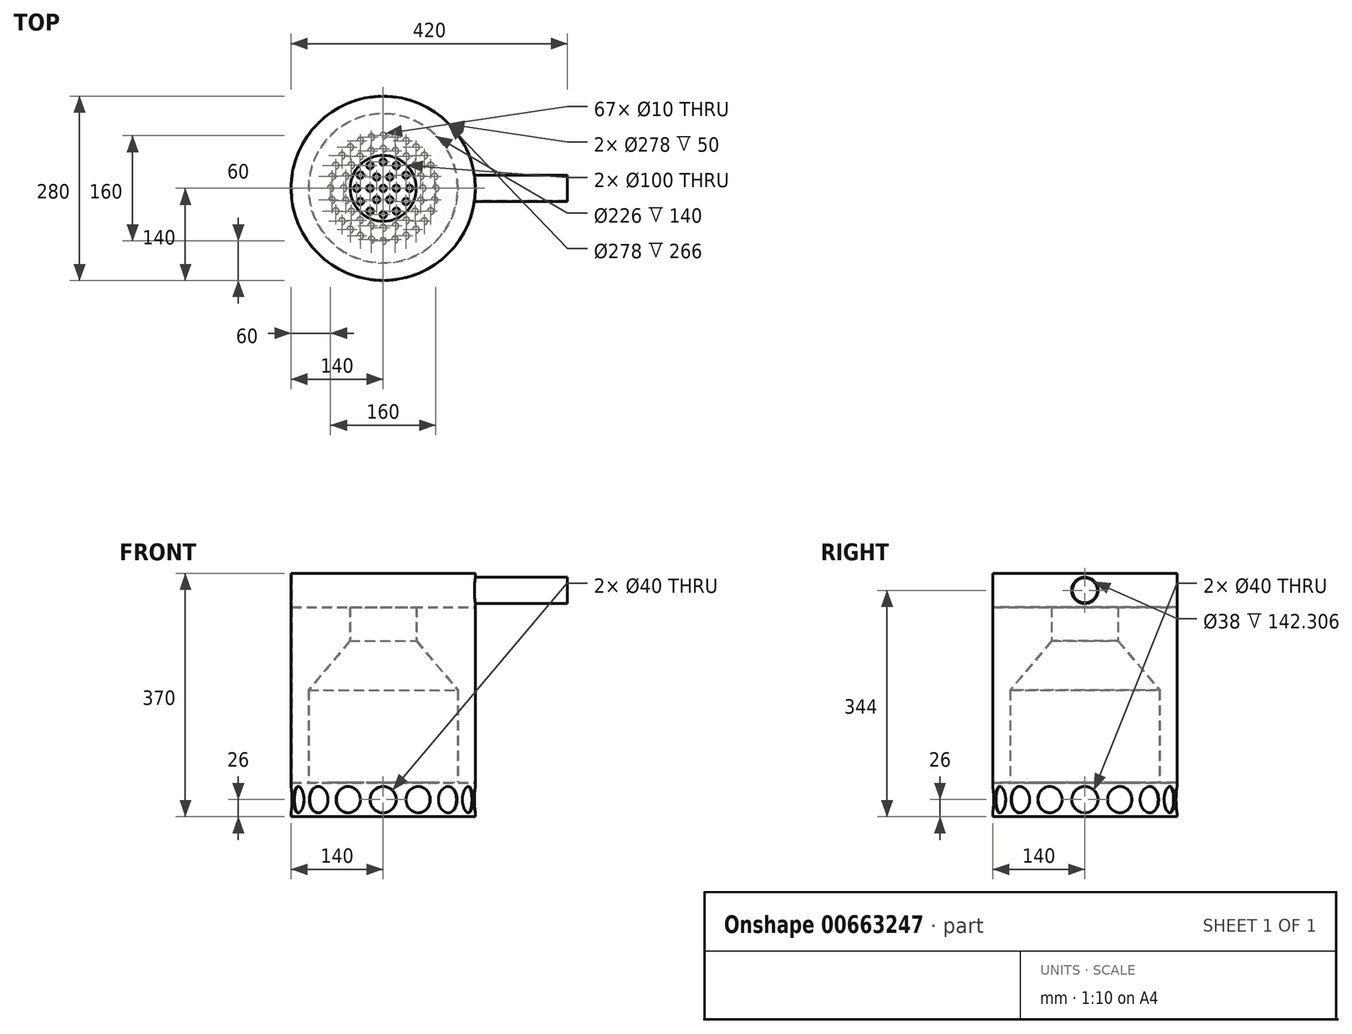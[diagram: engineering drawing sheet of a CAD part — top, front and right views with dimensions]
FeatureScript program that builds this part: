
annotation { "Feature Type Name" : "Feature", "Feature Type Description" : "" }
export const myFeature = defineFeature(function(context is Context, id is Id, definition is map)
    precondition{}
    {
        {
            var Q0;
            Q0=qCreatedBy(makeId("Front.planeOp"),FACE);
            var sketch = newSketch(context, id + "F0", { "sketchPlane" : qUnion([Q0])});
            skLineSegment(sketch, "E0", {"start": v(0, 0) * mm, "end": v(140, 0) * mm});
            skLineSegment(sketch, "E1", {"start": v(140, 0) * mm, "end": v(140, 370) * mm});
            skLineSegment(sketch, "E2", {"start": v(140, 370) * mm, "end": v(50, 370) * mm});
            skLineSegment(sketch, "E3.0", {"start": v(139, 369) * mm, "end": v(50, 369) * mm});
            skLineSegment(sketch, "E3.1", {"start": v(139, 1) * mm, "end": v(139, 369) * mm});
            skLineSegment(sketch, "E3.2", {"start": v(0, 1) * mm, "end": v(139, 1) * mm});
            skLineSegment(sketch, "E4", {"start": v(50, 370) * mm, "end": v(50, 369) * mm});
            skLineSegment(sketch, "E5", {"start": v(0, 1) * mm, "end": v(0, 0) * mm});
            skLineSegment(sketch, "E6", {"start": v(0, 51) * mm, "end": v(139, 51) * mm});
            skLineSegment(sketch, "E7", {"start": v(0, 51) * mm, "end": v(0, 52) * mm});
            skLineSegment(sketch, "E8", {"start": v(0, 52) * mm, "end": v(139, 52) * mm});
            skLineSegment(sketch, "E9", {"start": v(50, 319) * mm, "end": v(139, 319) * mm});
            skLineSegment(sketch, "E10", {"start": v(50, 319) * mm, "end": v(50, 318) * mm});
            skLineSegment(sketch, "E11", {"start": v(50, 318) * mm, "end": v(139, 318) * mm});
            skLineSegment(sketch, "E12", {"start": v(50, 318) * mm, "end": v(50, 267.08) * mm});
            skLineSegment(sketch, "E13", {"start": v(50, 267.08) * mm, "end": v(113, 192) * mm});
            skLineSegment(sketch, "E14", {"start": v(113, 192) * mm, "end": v(113, 52) * mm});
            skLineSegment(sketch, "E15.0", {"start": v(114, 192.36) * mm, "end": v(114, 52) * mm});
            skLineSegment(sketch, "E15.1", {"start": v(51, 267.44) * mm, "end": v(114, 192.36) * mm});
            skLineSegment(sketch, "E15.2", {"start": v(51, 318) * mm, "end": v(51, 267.44) * mm});
            skLineSegment(sketch, "E16", {"start": v(0, 0) * mm, "end": v(0, 370) * mm, "construction": true});
            skSolve(sketch);
        }
        {
            var Q0;
            Q0=makeQuery(id+"F0.imprint","IMPRINT",FACE,{"disambiguationData":[TD([[makeQuery(id+"F0.imprint","IMPRINT",EDGE,{"derivedFrom":sQuery(id+"F0.wireOp",EDGE,"E0")}),1.0]])]});
            var Q1;
            {var subQ3=sQuery(id+"F0.wireOp",EDGE,"E6");Q1=makeQuery(id+"F0.imprint","IMPRINT",FACE,{"disambiguationData":[TD([[makeQuery(id+"F0.imprint","IMPRINT",EDGE,{"derivedFrom":subQ3}),1.0]])]});}
            var Q2;
            {var subQ0=sQuery(id+"F0.wireOp",EDGE,"E12");Q2=makeQuery(id+"F0.imprint","IMPRINT",FACE,{"disambiguationData":[TD([[makeQuery(id+"F0.imprint","IMPRINT",EDGE,{"derivedFrom":subQ0}),1.0]])]});}
            var Q3;
            {var subQ3=sQuery(id+"F0.wireOp",EDGE,"E9");Q3=makeQuery(id+"F0.imprint","IMPRINT",FACE,{"disambiguationData":[TD([[makeQuery(id+"F0.imprint","IMPRINT",EDGE,{"derivedFrom":subQ3}),-1.0]])]});}
            var Q4;
            Q4=sQuery(id+"F0.wireOp",EDGE,"E16");
            revolve(context, id + "F1", {"entities" : qUnion([Q0, Q1, Q2, Q3]), "axis" : qUnion([Q4]), "revolveType" : RevolveType.FULL});
        }
        {
            var Q0;
            {var subQ0=sQuery(id+"F0.wireOp",EDGE,"E8");Q0=makeQuery(id+"F1.opRevolve","SWEPT_FACE",FACE,{"disambiguationData":[OSD([subQ0]),TDD([makeQuery(id+"F0.imprint","IMPRINT",EDGE,{"disambiguationData":[TD([[makeQuery(id+"F0.imprint","INTERSECT",VERTEX,{"derivedFrom":[sQuery(id+"F0.wireOp",EDGE,"E7"),subQ0]}),-1.0]])],"derivedFrom":subQ0})])]});}
            var sketch = newSketch(context, id + "F2", { "sketchPlane" : qUnion([Q0])});
            skCircle(sketch, "E17", {"center": v(0, 0) * mm, "radius": 5 * mm});
            skCircle(sketch, "E18", {"center": v(20, 0) * mm, "radius": 5 * mm});
            skCircle(sketch, "E19.1.0", {"center": v(10, 17.32) * mm, "radius": 5 * mm});
            skCircle(sketch, "E19.2.0", {"center": v(-10, 17.32) * mm, "radius": 5 * mm});
            skCircle(sketch, "E20.1.3.0", {"center": v(-20, 0) * mm, "radius": 5 * mm});
            skCircle(sketch, "E21", {"center": v(40, 0) * mm, "radius": 5 * mm});
            skCircle(sketch, "E22.1.0", {"center": v(34.64, 20) * mm, "radius": 5 * mm});
            skCircle(sketch, "E22.2.0", {"center": v(20, 34.64) * mm, "radius": 5 * mm});
            skCircle(sketch, "E23.1.3.0", {"center": v(0, 40) * mm, "radius": 5 * mm});
            skCircle(sketch, "E23.1.4.0", {"center": v(-20, 34.64) * mm, "radius": 5 * mm});
            skCircle(sketch, "E23.1.5.0", {"center": v(-34.64, 20) * mm, "radius": 5 * mm});
            skCircle(sketch, "E23.1.6.0", {"center": v(-40, 0) * mm, "radius": 5 * mm});
            skCircle(sketch, "E23.1.7.0", {"center": v(-34.64, -20) * mm, "radius": 5 * mm});
            skCircle(sketch, "E24", {"center": v(60, 0) * mm, "radius": 5 * mm});
            skCircle(sketch, "E25", {"center": v(80, 0) * mm, "radius": 5 * mm});
            skCircle(sketch, "E26.1.0", {"center": v(57.06, 18.54) * mm, "radius": 5 * mm});
            skCircle(sketch, "E26.2.0", {"center": v(48.54, 35.27) * mm, "radius": 5 * mm});
            skCircle(sketch, "E27.1.3.0", {"center": v(35.27, 48.54) * mm, "radius": 5 * mm});
            skCircle(sketch, "E27.1.4.0", {"center": v(18.54, 57.06) * mm, "radius": 5 * mm});
            skCircle(sketch, "E27.1.5.0", {"center": v(0, 60) * mm, "radius": 5 * mm});
            skCircle(sketch, "E27.1.6.0", {"center": v(-18.54, 57.06) * mm, "radius": 5 * mm});
            skCircle(sketch, "E27.1.7.0", {"center": v(-35.27, 48.54) * mm, "radius": 5 * mm});
            skCircle(sketch, "E27.1.8.0", {"center": v(-48.54, 35.27) * mm, "radius": 5 * mm});
            skCircle(sketch, "E27.1.9.0", {"center": v(-57.06, 18.54) * mm, "radius": 5 * mm});
            skCircle(sketch, "E27.1.10.0", {"center": v(-60, 0) * mm, "radius": 5 * mm});
            skCircle(sketch, "E27.1.11.0", {"center": v(-57.06, -18.54) * mm, "radius": 5 * mm});
            skCircle(sketch, "E27.1.12.0", {"center": v(-48.54, -35.27) * mm, "radius": 5 * mm});
            skCircle(sketch, "E27.1.13.0", {"center": v(-35.27, -48.54) * mm, "radius": 5 * mm});
            skCircle(sketch, "E27.1.14.0", {"center": v(-18.54, -57.06) * mm, "radius": 5 * mm});
            skCircle(sketch, "E27.1.15.0", {"center": v(0, -60) * mm, "radius": 5 * mm});
            skCircle(sketch, "E27.1.16.0", {"center": v(18.54, -57.06) * mm, "radius": 5 * mm});
            skCircle(sketch, "E27.1.17.0", {"center": v(35.27, -48.54) * mm, "radius": 5 * mm});
            skCircle(sketch, "E27.1.18.0", {"center": v(48.54, -35.27) * mm, "radius": 5 * mm});
            skCircle(sketch, "E27.1.19.0", {"center": v(57.06, -18.54) * mm, "radius": 5 * mm});
            skCircle(sketch, "E28.1.8.0", {"center": v(-20, -34.64) * mm, "radius": 5 * mm});
            skCircle(sketch, "E28.1.9.0", {"center": v(0, -40) * mm, "radius": 5 * mm});
            skCircle(sketch, "E28.1.10.0", {"center": v(20, -34.64) * mm, "radius": 5 * mm});
            skCircle(sketch, "E28.1.11.0", {"center": v(34.64, -20) * mm, "radius": 5 * mm});
            skCircle(sketch, "E29.1.0", {"center": v(78, 17.8) * mm, "radius": 5 * mm});
            skCircle(sketch, "E29.2.0", {"center": v(72.08, 34.71) * mm, "radius": 5 * mm});
            skCircle(sketch, "E30.1.3.0", {"center": v(62.55, 49.88) * mm, "radius": 5 * mm});
            skCircle(sketch, "E30.1.4.0", {"center": v(49.88, 62.55) * mm, "radius": 5 * mm});
            skCircle(sketch, "E30.1.5.0", {"center": v(34.71, 72.08) * mm, "radius": 5 * mm});
            skCircle(sketch, "E30.1.6.0", {"center": v(17.8, 78) * mm, "radius": 5 * mm});
            skCircle(sketch, "E30.1.7.0", {"center": v(0, 80) * mm, "radius": 5 * mm});
            skCircle(sketch, "E30.1.8.0", {"center": v(-17.8, 78) * mm, "radius": 5 * mm});
            skCircle(sketch, "E30.1.9.0", {"center": v(-34.71, 72.08) * mm, "radius": 5 * mm});
            skCircle(sketch, "E30.1.10.0", {"center": v(-49.88, 62.55) * mm, "radius": 5 * mm});
            skCircle(sketch, "E30.1.11.0", {"center": v(-62.55, 49.88) * mm, "radius": 5 * mm});
            skCircle(sketch, "E30.1.12.0", {"center": v(-72.08, 34.71) * mm, "radius": 5 * mm});
            skCircle(sketch, "E30.1.13.0", {"center": v(-78, 17.8) * mm, "radius": 5 * mm});
            skCircle(sketch, "E30.1.14.0", {"center": v(-80, 0) * mm, "radius": 5 * mm});
            skCircle(sketch, "E30.1.15.0", {"center": v(-78, -17.8) * mm, "radius": 5 * mm});
            skCircle(sketch, "E30.1.16.0", {"center": v(-72.08, -34.71) * mm, "radius": 5 * mm});
            skCircle(sketch, "E30.1.17.0", {"center": v(-62.55, -49.88) * mm, "radius": 5 * mm});
            skCircle(sketch, "E30.1.18.0", {"center": v(-49.88, -62.55) * mm, "radius": 5 * mm});
            skCircle(sketch, "E30.1.19.0", {"center": v(-34.71, -72.08) * mm, "radius": 5 * mm});
            skCircle(sketch, "E30.1.20.0", {"center": v(-17.8, -78) * mm, "radius": 5 * mm});
            skCircle(sketch, "E30.1.21.0", {"center": v(0, -80) * mm, "radius": 5 * mm});
            skCircle(sketch, "E30.1.22.0", {"center": v(17.8, -78) * mm, "radius": 5 * mm});
            skCircle(sketch, "E30.1.23.0", {"center": v(34.71, -72.08) * mm, "radius": 5 * mm});
            skCircle(sketch, "E30.1.24.0", {"center": v(49.88, -62.55) * mm, "radius": 5 * mm});
            skCircle(sketch, "E30.1.25.0", {"center": v(62.55, -49.88) * mm, "radius": 5 * mm});
            skCircle(sketch, "E30.1.26.0", {"center": v(72.08, -34.71) * mm, "radius": 5 * mm});
            skCircle(sketch, "E30.1.27.0", {"center": v(78, -17.8) * mm, "radius": 5 * mm});
            skCircle(sketch, "E31.1.4.0", {"center": v(-10, -17.32) * mm, "radius": 5 * mm});
            skCircle(sketch, "E31.1.5.0", {"center": v(10, -17.32) * mm, "radius": 5 * mm});
            skSolve(sketch);
        }
        {
            var Q0;
            Q0 = qSketchRegion(id + "F2", true);
            extrude(context, id + "F3", {"entities" : qUnion([Q0]), "operationType" : NewBodyOperationType.REMOVE, "oppositeDirection" : true, "depth" : 1 * mm, "offsetDistance" : 25 * mm});
        }
        {
            var Q0;
            Q0=qCreatedBy(makeId("Right.planeOp"),FACE);
            var sketch = newSketch(context, id + "F4", { "sketchPlane" : qUnion([Q0])});
            skCircle(sketch, "E32", {"center": v(0, 344) * mm, "radius": 20 * mm});
            skSolve(sketch);
        }
        {
            var Q0;
            Q0=makeQuery(id+"F4.imprint","IMPRINT",FACE,{"disambiguationData":[TD([[makeQuery(id+"F4.imprint","IMPRINT",EDGE,{"derivedFrom":sQuery(id+"F4.wireOp",EDGE,"E32")}),1.0]])]});
            var Q1;
            Q1=sQuery(id+"F4.wireOp",EDGE,"E32");
            extrude(context, id + "F5", {"entities" : qUnion([Q0]), "operationType" : NewBodyOperationType.ADD, "surfaceEntities" : qUnion([Q1]), "depth" : 280 * mm, "offsetDistance" : 25 * mm});
        }
        {
            var Q0;
            Q0=makeQuery(id+"F5.opExtrude","CAP_FACE",FACE,{"disambiguationData":[OSD([sQuery(id+"F4.wireOp",EDGE,"E32")])],"isStart":true});
            var sketch = newSketch(context, id + "F6", { "sketchPlane" : qUnion([Q0])});
            skCircle(sketch, "E33", {"center": v(0, 344) * mm, "radius": 19 * mm});
            skSolve(sketch);
        }
        {
            var Q0;
            Q0=makeQuery(id+"F6.imprint","IMPRINT",FACE,{"disambiguationData":[TD([[makeQuery(id+"F6.imprint","IMPRINT",EDGE,{"derivedFrom":sQuery(id+"F6.wireOp",EDGE,"E33")}),1.0]])]});
            extrude(context, id + "F7", {"entities" : qUnion([Q0]), "operationType" : NewBodyOperationType.REMOVE, "endBound" : BoundingType.THROUGH_ALL, "oppositeDirection" : true, "depth" : 25 * mm, "offsetDistance" : 25 * mm});
        }
        {
            var Q0;
            Q0=makeQuery(id+"F1.opRevolve","SWEPT_FACE",FACE,{"disambiguationData":[OSD([sQuery(id+"F0.wireOp",EDGE,"E9")])]});
            var sketch = newSketch(context, id + "F8", { "sketchPlane" : qUnion([Q0])});
            skCircle(sketch, "E34", {"center": v(0, 0) * mm, "radius": 139 * mm});
            skSolve(sketch);
        }
        {
            var Q0;
            Q0 = qSketchRegion(id + "F8", true);
            var Q1;
            Q1=makeQuery(id+"F1.opRevolve","SWEPT_FACE",FACE,{"disambiguationData":[OSD([sQuery(id+"F0.wireOp",EDGE,"E3.0")])]});
            extrude(context, id + "F9", {"entities" : qUnion([Q0]), "operationType" : NewBodyOperationType.REMOVE, "endBound" : BoundingType.UP_TO_SURFACE, "depth" : 25 * mm, "endBoundEntityFace" : qUnion([Q1]), "offsetDistance" : 25 * mm});
        }
        {
            var Q0;
            Q0=qCreatedBy(makeId("Front.planeOp"),FACE);
            var sketch = newSketch(context, id + "F10", { "sketchPlane" : qUnion([Q0])});
            skCircle(sketch, "E35", {"center": v(0, 26) * mm, "radius": 20 * mm});
            skSolve(sketch);
        }
        {
            var Q0;
            Q0 = qSketchRegion(id + "F10", true);
            extrude(context, id + "F11", {"entities" : qUnion([Q0]), "oppositeDirection" : true, "depth" : 150 * mm, "offsetDistance" : 25 * mm});
        }
        {
            var Q0;
            Q0=makeQuery(id+"F11.opExtrude","SWEPT_BODY",BODY,{"disambiguationData":[OSD([sQuery(id+"F10.wireOp",EDGE,"E35")])]});
            var Q1;
            Q1=sQuery(id+"F0.wireOp",EDGE,"E16");
            circularPattern(context, id + "F12", {"entities" : qUnion([Q0]), "axis" : qUnion([Q1]), "angle" : 360 * degree, "instanceCount" : 16, "equalSpace" : true});
        }
        {
            var Q0;
            Q0=makeQuery(id+"F11.opExtrude","SWEPT_BODY",BODY,{"disambiguationData":[OSD([sQuery(id+"F10.wireOp",EDGE,"E35")])]});
            var Q1;
            Q1=makeQuery(id+"F12.opPattern","COPY",BODY,{"derivedFrom":makeQuery(id+"F11.opExtrude","SWEPT_BODY",BODY,{"disambiguationData":[OSD([sQuery(id+"F10.wireOp",EDGE,"E35")])]}),"instanceName":"1"});
            var Q2;
            Q2=makeQuery(id+"F12.opPattern","COPY",BODY,{"derivedFrom":makeQuery(id+"F11.opExtrude","SWEPT_BODY",BODY,{"disambiguationData":[OSD([sQuery(id+"F10.wireOp",EDGE,"E35")])]}),"instanceName":"2"});
            var Q3;
            Q3=makeQuery(id+"F12.opPattern","COPY",BODY,{"derivedFrom":makeQuery(id+"F11.opExtrude","SWEPT_BODY",BODY,{"disambiguationData":[OSD([sQuery(id+"F10.wireOp",EDGE,"E35")])]}),"instanceName":"3"});
            var Q4;
            Q4=makeQuery(id+"F12.opPattern","COPY",BODY,{"derivedFrom":makeQuery(id+"F11.opExtrude","SWEPT_BODY",BODY,{"disambiguationData":[OSD([sQuery(id+"F10.wireOp",EDGE,"E35")])]}),"instanceName":"4"});
            var Q5;
            Q5=makeQuery(id+"F12.opPattern","COPY",BODY,{"derivedFrom":makeQuery(id+"F11.opExtrude","SWEPT_BODY",BODY,{"disambiguationData":[OSD([sQuery(id+"F10.wireOp",EDGE,"E35")])]}),"instanceName":"5"});
            var Q6;
            Q6=makeQuery(id+"F12.opPattern","COPY",BODY,{"derivedFrom":makeQuery(id+"F11.opExtrude","SWEPT_BODY",BODY,{"disambiguationData":[OSD([sQuery(id+"F10.wireOp",EDGE,"E35")])]}),"instanceName":"6"});
            var Q7;
            Q7=makeQuery(id+"F12.opPattern","COPY",BODY,{"derivedFrom":makeQuery(id+"F11.opExtrude","SWEPT_BODY",BODY,{"disambiguationData":[OSD([sQuery(id+"F10.wireOp",EDGE,"E35")])]}),"instanceName":"7"});
            var Q8;
            Q8=makeQuery(id+"F12.opPattern","COPY",BODY,{"derivedFrom":makeQuery(id+"F11.opExtrude","SWEPT_BODY",BODY,{"disambiguationData":[OSD([sQuery(id+"F10.wireOp",EDGE,"E35")])]}),"instanceName":"8"});
            var Q9;
            Q9=makeQuery(id+"F12.opPattern","COPY",BODY,{"derivedFrom":makeQuery(id+"F11.opExtrude","SWEPT_BODY",BODY,{"disambiguationData":[OSD([sQuery(id+"F10.wireOp",EDGE,"E35")])]}),"instanceName":"9"});
            var Q10;
            Q10=makeQuery(id+"F12.opPattern","COPY",BODY,{"derivedFrom":makeQuery(id+"F11.opExtrude","SWEPT_BODY",BODY,{"disambiguationData":[OSD([sQuery(id+"F10.wireOp",EDGE,"E35")])]}),"instanceName":"10"});
            var Q11;
            Q11=makeQuery(id+"F12.opPattern","COPY",BODY,{"derivedFrom":makeQuery(id+"F11.opExtrude","SWEPT_BODY",BODY,{"disambiguationData":[OSD([sQuery(id+"F10.wireOp",EDGE,"E35")])]}),"instanceName":"11"});
            var Q12;
            Q12=makeQuery(id+"F12.opPattern","COPY",BODY,{"derivedFrom":makeQuery(id+"F11.opExtrude","SWEPT_BODY",BODY,{"disambiguationData":[OSD([sQuery(id+"F10.wireOp",EDGE,"E35")])]}),"instanceName":"12"});
            var Q13;
            Q13=makeQuery(id+"F12.opPattern","COPY",BODY,{"derivedFrom":makeQuery(id+"F11.opExtrude","SWEPT_BODY",BODY,{"disambiguationData":[OSD([sQuery(id+"F10.wireOp",EDGE,"E35")])]}),"instanceName":"13"});
            var Q14;
            Q14=makeQuery(id+"F12.opPattern","COPY",BODY,{"derivedFrom":makeQuery(id+"F11.opExtrude","SWEPT_BODY",BODY,{"disambiguationData":[OSD([sQuery(id+"F10.wireOp",EDGE,"E35")])]}),"instanceName":"14"});
            var Q15;
            Q15=makeQuery(id+"F12.opPattern","COPY",BODY,{"derivedFrom":makeQuery(id+"F11.opExtrude","SWEPT_BODY",BODY,{"disambiguationData":[OSD([sQuery(id+"F10.wireOp",EDGE,"E35")])]}),"instanceName":"15"});
            var Q16;
            Q16=makeQuery(id+"F1.opRevolve","SWEPT_BODY",BODY,{"disambiguationData":[OSD([sQuery(id+"F0.wireOp",EDGE,"E0"),sQuery(id+"F0.wireOp",EDGE,"E1"),sQuery(id+"F0.wireOp",EDGE,"E2"),sQuery(id+"F0.wireOp",EDGE,"E3.0"),sQuery(id+"F0.wireOp",EDGE,"E3.1"),sQuery(id+"F0.wireOp",EDGE,"E3.2"),sQuery(id+"F0.wireOp",EDGE,"E4"),sQuery(id+"F0.wireOp",EDGE,"E5"),sQuery(id+"F0.wireOp",EDGE,"E6"),sQuery(id+"F0.wireOp",EDGE,"E7"),sQuery(id+"F0.wireOp",EDGE,"E8"),sQuery(id+"F0.wireOp",EDGE,"E9"),sQuery(id+"F0.wireOp",EDGE,"E10"),sQuery(id+"F0.wireOp",EDGE,"E11"),sQuery(id+"F0.wireOp",EDGE,"E12"),sQuery(id+"F0.wireOp",EDGE,"E13"),sQuery(id+"F0.wireOp",EDGE,"E14"),sQuery(id+"F0.wireOp",EDGE,"E15.0"),sQuery(id+"F0.wireOp",EDGE,"E15.1"),sQuery(id+"F0.wireOp",EDGE,"E15.2")])]});
            booleanBodies(context, id + "F13", {"operationType" : BooleanOperationType.SUBTRACTION, "tools" : qUnion([Q0, Q1, Q2, Q3, Q4, Q5, Q6, Q7, Q8, Q9, Q10, Q11, Q12, Q13, Q14, Q15]), "targets" : qUnion([Q16])});
        }
    });
